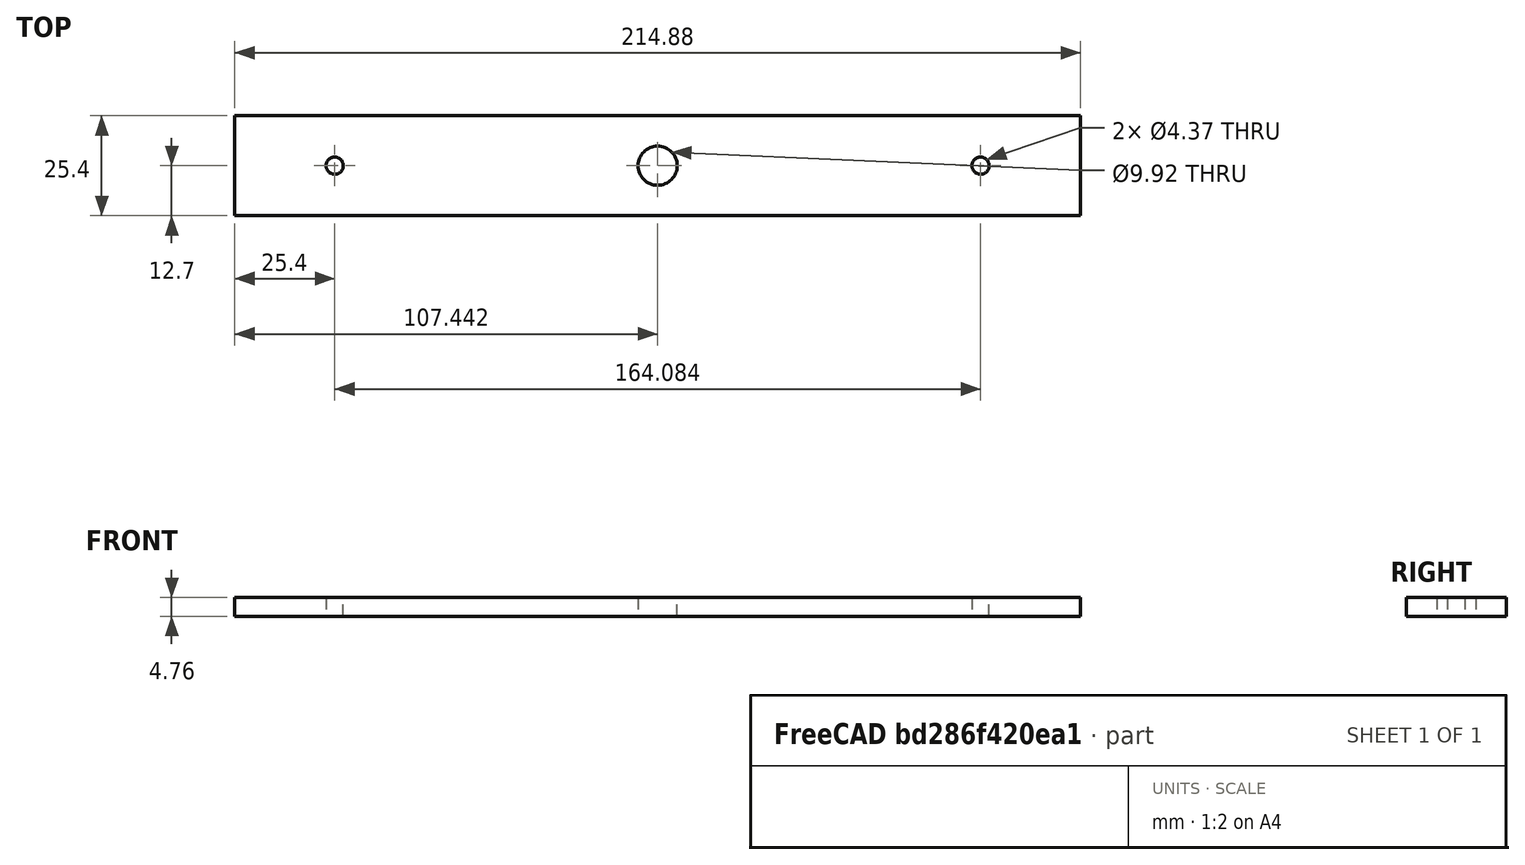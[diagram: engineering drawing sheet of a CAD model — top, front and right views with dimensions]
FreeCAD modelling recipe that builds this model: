
FCSTD DOCUMENT  (FreeCAD 0.19R24291 (Git))
Label: mirror_cell_bars
License: All rights reserved
LicenseURL: http://en.wikipedia.org/wiki/All_rights_reserved
objects: Sketcher::SketchObject×1, PartDesign::Body×1, Part::Feature×1, Part::Extrusion×1
note: 4 computed .brp shape members not serialized (recipe doc carries the construction recipe); baked Part::Feature solids carry a one-line shape summary decoded from their .brp

FEATURE [Sketcher::SketchObject] Sketch
  FullyConstrained = true
  MapMode = 5
  Support = -> [XY_Plane]
  sketch-geometry (17):
    g0: LineSegment StartX=0 StartY=0 StartZ=0 EndX=214.884 EndY=0 EndZ=0
    g1: LineSegment StartX=214.884 StartY=0 StartZ=0 EndX=214.884 EndY=25.4 EndZ=0
    g2: LineSegment StartX=214.884 StartY=25.4 StartZ=0 EndX=0 EndY=25.4 EndZ=0
    g3: LineSegment StartX=0 StartY=25.4 StartZ=0 EndX=0 EndY=0 EndZ=0
    g4: LineSegment StartX=0 StartY=25.4 StartZ=0 EndX=214.884 EndY=0 EndZ=0
    g5: LineSegment StartX=214.884 StartY=25.4 StartZ=0 EndX=0 EndY=0 EndZ=0
    g6: GeomPoint X=107.442 Y=12.7 Z=0
    g7: Circle CenterX=107.442 CenterY=12.7 CenterZ=0 NormalX=0 NormalY=0 NormalZ=1 AngleXU=0 Radius=4.96094
    g8: Circle CenterX=0 CenterY=25.4 CenterZ=0 NormalX=0 NormalY=0 NormalZ=1 AngleXU=0 Radius=25.4
    g9: Circle CenterX=0 CenterY=0 CenterZ=0 NormalX=0 NormalY=0 NormalZ=1 AngleXU=0 Radius=25.4
    g10: Circle CenterX=214.884 CenterY=25.4 CenterZ=0 NormalX=0 NormalY=0 NormalZ=1 AngleXU=0 Radius=25.4
    g11: Circle CenterX=214.884 CenterY=0 CenterZ=0 NormalX=0 NormalY=0 NormalZ=1 AngleXU=0 Radius=25.4
    g12: GeomPoint X=-21.997 Y=12.7 Z=0
    g13: GeomPoint X=236.881 Y=12.7 Z=0
    g14: LineSegment StartX=-21.997 StartY=12.7 StartZ=0 EndX=236.881 EndY=12.7 EndZ=0
    g15: Circle CenterX=25.4 CenterY=12.7 CenterZ=0 NormalX=0 NormalY=0 NormalZ=1 AngleXU=0 Radius=2.18281
    g16: Circle CenterX=189.484 CenterY=12.7 CenterZ=0 NormalX=0 NormalY=0 NormalZ=1 AngleXU=0 Radius=2.18281
  constraints (40):
    c: Coincident(g0,g1)
    c: Coincident(g1,g2)
    c: Coincident(g2,g3)
    c: Coincident(g3,g0)
    c: Horizontal(g0)
    c: Horizontal(g2)
    c: Vertical(g1)
    c: Vertical(g3)
    c: Coincident(g0,g-1)
    c: Distance(g2) = 214.884
    c: Distance(g1) = 25.4
    c: Coincident(g4,g2)
    c: Coincident(g4,g0)
    c: Coincident(g5,g1)
    c: Coincident(g5,g0)
    c: PointOnObject(g6,g5)
    c: PointOnObject(g6,g4)
    c: Coincident(g7,g6)
    c: Radius(g7) = 4.96094
    c: Coincident(g8,g2)
    c: PointOnObject(g0,g8)
    c: Coincident(g9,g0)
    c: PointOnObject(g2,g9)
    c: Coincident(g10,g1)
    c: PointOnObject(g0,g10)
    c: Coincident(g11,g0)
    c: PointOnObject(g1,g11)
    c: PointOnObject(g12,g8)
    c: PointOnObject(g13,g10)
    c: PointOnObject(g12,g9)
    c: PointOnObject(g13,g11)
    c: Coincident(g14,g12)
    c: Coincident(g14,g13)
    c: PointOnObject(g15,g14)
    c: Radius(g15) = 2.18281
    c: Distance(g15,g3) = 25.4
    c: PointOnObject(g16,g14)
    c: Distance(g16,g1) = 25.4
    c: Block(g16)
    c: Radius(g16) = 2.18281
FEATURE [PartDesign::Body] Body
  Group = -> [Sketch]
  Origin = -> Origin
FEATURE [Part::Feature] Part
FEATURE [Part::Extrusion] Extrude
  Base = -> Sketch
  Dir = (0,0,1)
  DirMode = 2
  FaceMakerClass = Part::FaceMakerBullseye
  LengthFwd = 4.7625
  LengthRev = 0
  Solid = true
  Symmetric = false
